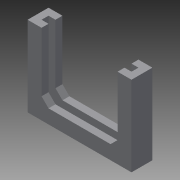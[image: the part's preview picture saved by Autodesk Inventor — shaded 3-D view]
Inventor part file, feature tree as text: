
AUTODESK INVENTOR PART (.ipt)
format: ipt  version: 2015 (Build 190159000, 159)  size: 111,104 bytes
history: native  units: mm
features: extrude x3, sketch x3, chamfer x1
ambient origin geometry x8: Origin, YZ Plane, XZ Plane, XY Plane, X Axis, Y Axis, Z Axis, Center Point
bodies: Body1 (feature_tree)
feature tree (7):
  extrude  "Extrusion5"  Depth=2.0mm
  extrude  "Extrusion6"  Depth=2.0mm
  extrude  "Extrusion7"  Depth=2.0mm
  chamfer  "Chamfer1"  Distance=23.0mm
  sketch  "Sketch1"  dims[d0=25.8mm d1=2.0mm]
  sketch  "Sketch4"  dims[d4=2.0mm d5=2.0mm]
  sketch  "Sketch5"  dims[d6=2.0mm d7=2.0mm d18=23.0mm d19=0.0mm d20=2.0mm d21=2.0mm d22=2.0mm d23=2.0mm d24=21.0mm d25=0.0mm d26=4.0mm d27=4.0mm d28=4.0mm d29=22.0mm d30=0.0mm d32=2.0mm d33=2.0mm d34=45.0deg]
